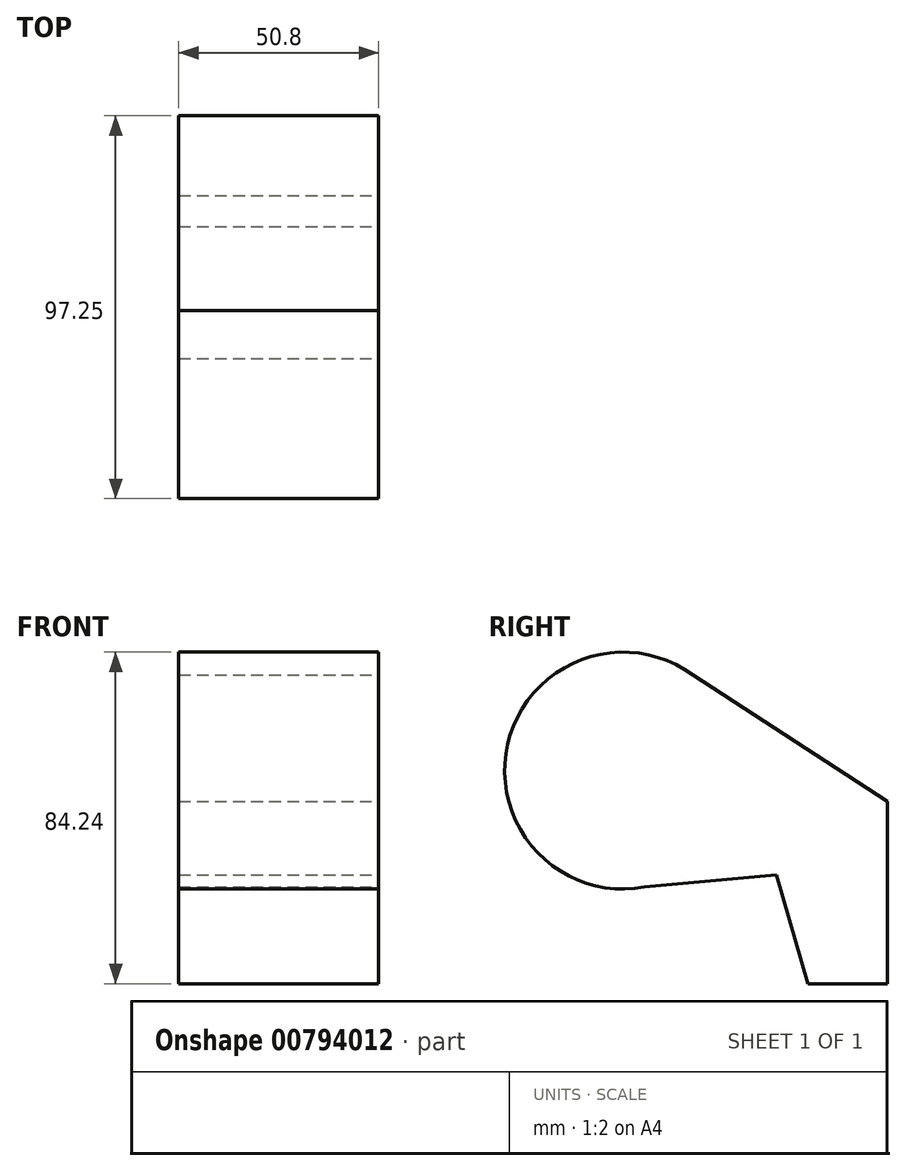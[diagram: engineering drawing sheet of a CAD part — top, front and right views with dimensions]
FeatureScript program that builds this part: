
annotation { "Feature Type Name" : "Feature", "Feature Type Description" : "" }
export const myFeature = defineFeature(function(context is Context, id is Id, definition is map)
    precondition{}
    {
        {
            var Q0;
            Q0=qCreatedBy(makeId("Right.planeOp"),FACE);
            var sketch = newSketch(context, id + "F0", { "sketchPlane" : qUnion([Q0])});
            skArc(sketch, "E0", {"start": v(-11.47, 59.72) * mm, "mid": v(-58.54, 42.07) * mm, "end": v(-23.75, 5.79) * mm});
            skLineSegment(sketch, "E1.top", {"start": v(17.7, -18.75) * mm, "end": v(37.96, -18.75) * mm});
            skLineSegment(sketch, "E1.right", {"start": v(37.96, 27.53) * mm, "end": v(37.96, -18.75) * mm});
            skLineSegment(sketch, "E2", {"start": v(-11.47, 59.72) * mm, "end": v(37.96, 27.53) * mm});
            skLineSegment(sketch, "E3", {"start": v(17.7, -18.75) * mm, "end": v(9.76, 8.84) * mm});
            skLineSegment(sketch, "E4", {"start": v(9.76, 8.84) * mm, "end": v(-29.2, 5.3) * mm});
            skSolve(sketch);
        }
        {
            var Q0;
            Q0 = qSketchRegion(id + "F0", true);
            extrude(context, id + "F1", {"entities" : qUnion([Q0]), "depth" : -50.8 * mm, "offsetDistance" : 25.4 * mm});
        }
    });
